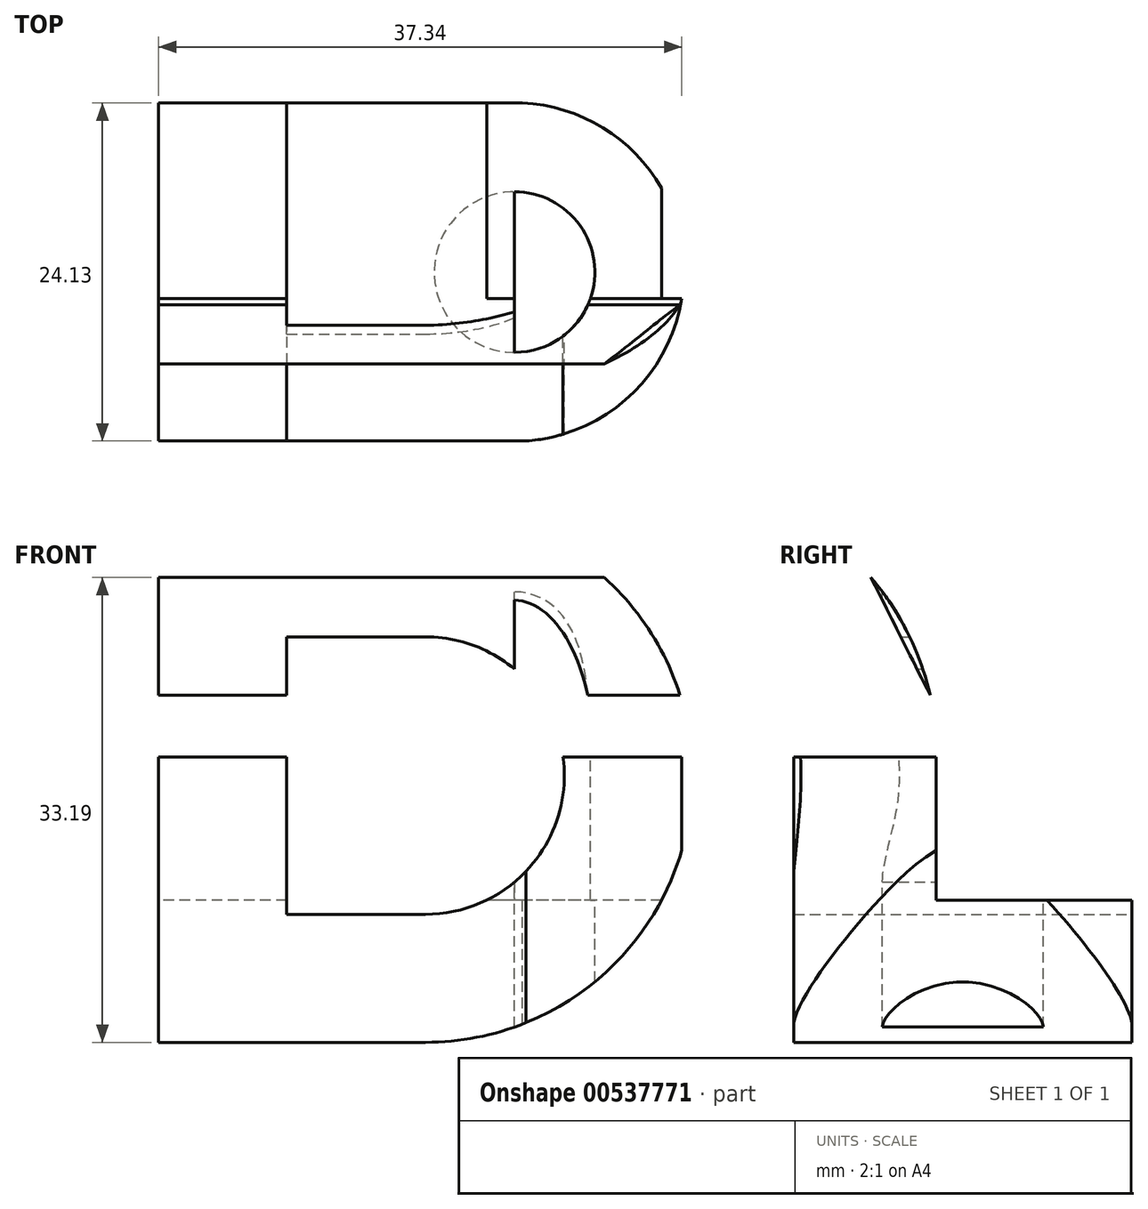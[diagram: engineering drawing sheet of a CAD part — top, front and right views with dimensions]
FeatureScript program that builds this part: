
annotation { "Feature Type Name" : "Feature", "Feature Type Description" : "" }
export const myFeature = defineFeature(function(context is Context, id is Id, definition is map)
    precondition{}
    {
        {
            var Q0;
            Q0=qCreatedBy(makeId("Front.planeOp"),FACE);
            var sketch = newSketch(context, id + "F0", { "sketchPlane" : qUnion([Q0])});
            skLineSegment(sketch, "E0", {"start": v(0, 0) * mm, "end": v(0, 38.1) * mm});
            skLineSegment(sketch, "E1.bottom", {"start": v(0, 0) * mm, "end": v(38.1, 0) * mm});
            skLineSegment(sketch, "E1.top", {"start": v(0, 38.1) * mm, "end": v(38.1, 38.1) * mm});
            skLineSegment(sketch, "E1.right", {"start": v(38.1, 0) * mm, "end": v(38.1, 38.1) * mm});
            skLineSegment(sketch, "E2", {"start": v(19.05, 38.1) * mm, "end": v(19.05, 0) * mm});
            skLineSegment(sketch, "E3", {"start": v(19.05, 0) * mm, "end": v(0, 0) * mm});
            skArc(sketch, "E4", {"start": v(19.05, 0) * mm, "mid": v(38.1, 19.05) * mm, "end": v(19.05, 38.1) * mm});
            skLineSegment(sketch, "E5", {"start": v(19.05, 38.1) * mm, "end": v(0, 38.1) * mm});
            skLineSegment(sketch, "E6.0", {"start": v(19.05, 28.96) * mm, "end": v(9.14, 28.96) * mm});
            skArc(sketch, "E6.1", {"start": v(19.05, 9.14) * mm, "mid": v(28.96, 19.05) * mm, "end": v(19.05, 28.96) * mm});
            skLineSegment(sketch, "E6.2", {"start": v(19.05, 9.14) * mm, "end": v(9.14, 9.14) * mm});
            skLineSegment(sketch, "E6.3", {"start": v(9.14, 9.14) * mm, "end": v(9.14, 28.96) * mm});
            skSolve(sketch);
        }
        {
            var Q0;
            Q0=makeQuery(id+"F0.imprint","IMPRINT",FACE,{"disambiguationData":[TD([[makeQuery(id+"F0.imprint","IMPRINT",EDGE,{"derivedFrom":sQuery(id+"F0.wireOp",EDGE,"E0")}),-1.0]])]});
            var Q1;
            {var subQ4=sQuery(id+"F0.wireOp",EDGE,"E6.1");Q1=makeQuery(id+"F0.imprint","IMPRINT",FACE,{"disambiguationData":[TD([[makeQuery(id+"F0.imprint","IMPRINT",EDGE,{"derivedFrom":subQ4}),-1.0]])]});}
            extrude(context, id + "F1", {"entities" : qUnion([Q0, Q1]), "depth" : 38.1 * mm, "offsetDistance" : 25.4 * mm});
        }
        {
            var Q0;
            Q0=qCreatedBy(makeId("Right.planeOp"),FACE);
            var sketch = newSketch(context, id + "F2", { "sketchPlane" : qUnion([Q0])});
            skLineSegment(sketch, "E7.bottom", {"start": v(-38.1, 38.1) * mm, "end": v(0, 38.1) * mm});
            skLineSegment(sketch, "E7.top", {"start": v(-38.1, 0) * mm, "end": v(0, 0) * mm});
            skLineSegment(sketch, "E7.left", {"start": v(-38.1, 38.1) * mm, "end": v(-38.1, 0) * mm});
            skLineSegment(sketch, "E7.right", {"start": v(0, 38.1) * mm, "end": v(0, 0) * mm});
            skLineSegment(sketch, "E8.top", {"start": v(-38.1, 10.16) * mm, "end": v(0, 10.16) * mm});
            skLineSegment(sketch, "E8.left", {"start": v(-38.1, 0) * mm, "end": v(-38.1, 10.16) * mm});
            skLineSegment(sketch, "E8.right", {"start": v(0, 0) * mm, "end": v(0, 10.16) * mm});
            skLineSegment(sketch, "E9.bottom", {"start": v(-13.97, 20.37) * mm, "end": v(-24.13, 20.37) * mm});
            skLineSegment(sketch, "E9.top", {"start": v(-13.97, -0.05) * mm, "end": v(-24.13, -0.05) * mm});
            skLineSegment(sketch, "E9.left", {"start": v(-13.97, 20.37) * mm, "end": v(-13.97, -0.05) * mm});
            skLineSegment(sketch, "E9.right", {"start": v(-24.13, 20.37) * mm, "end": v(-24.13, -0.05) * mm});
            skPoint(sketch, "E9.middle", {"position": v(-19.05, 10.16) * mm});
            skArc(sketch, "E10", {"start": v(-24.13, 20.37) * mm, "mid": v(-28.73, 28.53) * mm, "end": v(-38.1, 28.81) * mm});
            skArc(sketch, "E11.0", {"start": v(-13.9, 20.37) * mm, "mid": v(-23.44, 37.28) * mm, "end": v(-42.85, 37.87) * mm});
            skLineSegment(sketch, "E12.1", {"start": v(6.35, -6.35) * mm, "end": v(-44.45, -6.35) * mm});
            skLineSegment(sketch, "E13", {"start": v(-38.1, 28.81) * mm, "end": v(-38.1, 38.1) * mm});
            skLineSegment(sketch, "E14", {"start": v(-24.93, 38.1) * mm, "end": v(-18.63, 33.2) * mm});
            skLineSegment(sketch, "E15", {"start": v(-18.63, 33.2) * mm, "end": v(-14.4, 24.8) * mm});
            skLineSegment(sketch, "E16", {"start": v(-14.4, 24.8) * mm, "end": v(-13.97, 20.37) * mm});
            skLineSegment(sketch, "E17", {"start": v(-24.93, 38.1) * mm, "end": v(-38.1, 38.1) * mm});
            skSolve(sketch);
        }
        {
            var Q0;
            {var subQ5=sQuery(id+"F2.wireOp",EDGE,"E9.top");Q0=makeQuery(id+"F2.imprint","IMPRINT",FACE,{"disambiguationData":[TD([[makeQuery(id+"F2.imprint","IMPRINT",EDGE,{"derivedFrom":subQ5}),-1.0]])]});}
            var Q1;
            {var subQ0=sQuery(id+"F2.wireOp",EDGE,"E14");Q1=makeQuery(id+"F2.imprint","IMPRINT",FACE,{"disambiguationData":[TD([[makeQuery(id+"F2.imprint","IMPRINT",EDGE,{"derivedFrom":subQ0}),1.0]])]});}
            var Q2;
            {var subQ0=sQuery(id+"F2.wireOp",EDGE,"E7.left");Q2=makeQuery(id+"F2.imprint","IMPRINT",FACE,{"disambiguationData":[TD([[makeQuery(id+"F2.imprint","IMPRINT",EDGE,{"derivedFrom":subQ0}),1.0]])]});}
            var Q3;
            {var subQ5=sQuery(id+"F2.wireOp",EDGE,"E7.bottom");Q3=makeQuery(id+"F2.imprint","IMPRINT",FACE,{"disambiguationData":[TD([[makeQuery(id+"F2.imprint","IMPRINT",EDGE,{"derivedFrom":subQ5}),-1.0]])]});}
            extrude(context, id + "F3", {"entities" : qUnion([Q0, Q1, Q2, Q3]), "operationType" : NewBodyOperationType.REMOVE, "depth" : 38.1 * mm, "offsetDistance" : 25.4 * mm});
        }
        {
            var Q0;
            Q0=qCreatedBy(makeId("Top.planeOp"),FACE);
            cPlane(context, id + "F4", {"entities" : qUnion([Q0]), "cplaneType" : CPlaneType.OFFSET, "offset" : 38.1 * mm, "width" : 152.4 * mm, "height" : 152.4 * mm});
        }
        {
            var Q0;
            Q0=qCreatedBy(id+"F4.planeOp",FACE);
            var sketch = newSketch(context, id + "F5", { "sketchPlane" : qUnion([Q0])});
            skLineSegment(sketch, "E18.bottom", {"start": v(0, 0) * mm, "end": v(38.1, 0) * mm});
            skLineSegment(sketch, "E18.top", {"start": v(0, -38.1) * mm, "end": v(38.1, -38.1) * mm});
            skLineSegment(sketch, "E18.left", {"start": v(0, 0) * mm, "end": v(0, -38.1) * mm});
            skLineSegment(sketch, "E18.right", {"start": v(38.1, 0) * mm, "end": v(38.1, -38.1) * mm});
            skLineSegment(sketch, "E19", {"start": v(0, -38.1) * mm, "end": v(0, 0) * mm});
            skArc(sketch, "E20", {"start": v(25.4, -24.16) * mm, "mid": v(37.49, -12.07) * mm, "end": v(25.4, 0.01) * mm});
            skLineSegment(sketch, "E21.bottom", {"start": v(0, -38.1) * mm, "end": v(25.4, -38.1) * mm});
            skLineSegment(sketch, "E21.top", {"start": v(0, 0.01) * mm, "end": v(25.4, 0.01) * mm});
            skLineSegment(sketch, "E21.left", {"start": v(0, -38.1) * mm, "end": v(0, 0.01) * mm});
            skLineSegment(sketch, "E21.right", {"start": v(25.4, -38.1) * mm, "end": v(25.4, 0.01) * mm});
            skLineSegment(sketch, "E22", {"start": v(25.4, -24.16) * mm, "end": v(38.1, -38.1) * mm});
            skLineSegment(sketch, "E23", {"start": v(25.4, -35.02) * mm, "end": v(27.7, -38.1) * mm});
            skLineSegment(sketch, "E24", {"start": v(27.7, -38.1) * mm, "end": v(38.1, -38.1) * mm});
            skLineSegment(sketch, "E25", {"start": v(25.4, -35.02) * mm, "end": v(25.4, -24.16) * mm});
            skArc(sketch, "E26.0", {"start": v(25.4, -17.8) * mm, "mid": v(31.14, -12.07) * mm, "end": v(25.4, -6.34) * mm});
            skLineSegment(sketch, "E27", {"start": v(25.4, -17.8) * mm, "end": v(25.4, -6.34) * mm});
            skSolve(sketch);
        }
        {
            var Q0;
            {var subQ5=sQuery(id+"F5.wireOp",EDGE,"E21.top");Q0=makeQuery(id+"F5.imprint","IMPRINT",FACE,{"disambiguationData":[TD([[makeQuery(id+"F5.imprint","IMPRINT",EDGE,{"derivedFrom":subQ5}),-1.0]])]});}
            var Q1;
            {var subQ0=sQuery(id+"F5.wireOp",EDGE,"E20");var subQ1=sQuery(id+"F5.wireOp",EDGE,"E18.bottom");var subQ2=makeQuery(id+"F5.imprint","INTERSECT",VERTEX,{"derivedFrom":[subQ1,subQ0]});Q1=makeQuery(id+"F5.imprint","IMPRINT",FACE,{"disambiguationData":[TD([[makeQuery(id+"F5.imprint","IMPRINT",EDGE,{"disambiguationData":[TD([[subQ2,1.0]])],"derivedFrom":subQ1}),1.0]])]});}
            var Q2;
            {var subQ0=sQuery(id+"F5.wireOp",EDGE,"E18.right");Q2=makeQuery(id+"F5.imprint","IMPRINT",FACE,{"disambiguationData":[TD([[makeQuery(id+"F5.imprint","IMPRINT",EDGE,{"derivedFrom":subQ0}),-1.0]])]});}
            var Q3;
            {var subQ0=sQuery(id+"F5.wireOp",EDGE,"E18.top");Q3=makeQuery(id+"F5.imprint","IMPRINT",FACE,{"disambiguationData":[TD([[makeQuery(id+"F5.imprint","IMPRINT",EDGE,{"derivedFrom":subQ0}),1.0]])]});}
            var Q4;
            Q4=makeQuery(id+"F5.imprint","IMPRINT",FACE,{"disambiguationData":[TD([[makeQuery(id+"F5.imprint","IMPRINT",EDGE,{"derivedFrom":sQuery(id+"F5.wireOp",EDGE,"E26.0")}),1.0]])]});
            extrude(context, id + "F6", {"entities" : qUnion([Q0, Q1, Q2, Q3, Q4]), "operationType" : NewBodyOperationType.REMOVE, "oppositeDirection" : true, "depth" : 38.1 * mm, "offsetDistance" : 25.4 * mm});
        }
    });
